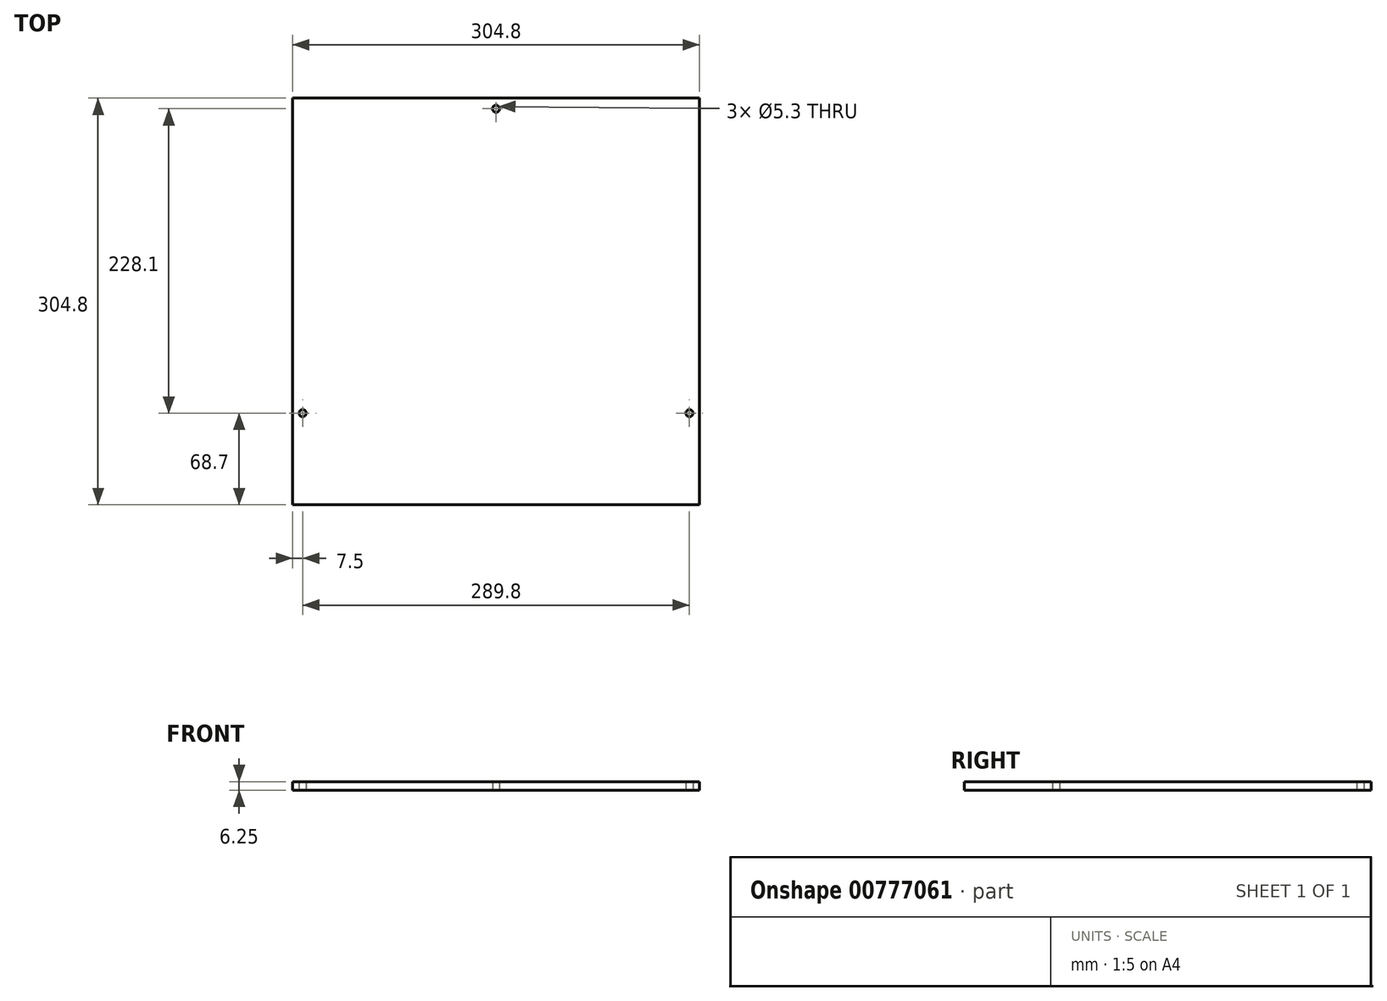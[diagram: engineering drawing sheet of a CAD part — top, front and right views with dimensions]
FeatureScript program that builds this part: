
annotation { "Feature Type Name" : "Feature", "Feature Type Description" : "" }
export const myFeature = defineFeature(function(context is Context, id is Id, definition is map)
    precondition{}
    {
        {
            var Q0;
            Q0=qCreatedBy(makeId("Top.planeOp"),FACE);
            var sketch = newSketch(context, id + "F0", { "sketchPlane" : qUnion([Q0])});
            skLineSegment(sketch, "E0.bottom", {"start": v(-152.4, 152.4) * mm, "end": v(152.4, 152.4) * mm});
            skLineSegment(sketch, "E0.top", {"start": v(-152.4, -152.4) * mm, "end": v(152.4, -152.4) * mm});
            skLineSegment(sketch, "E0.left", {"start": v(-152.4, 152.4) * mm, "end": v(-152.4, -152.4) * mm});
            skLineSegment(sketch, "E0.right", {"start": v(152.4, 152.4) * mm, "end": v(152.4, -152.4) * mm});
            skCircle(sketch, "E1", {"center": v(0, 144.4) * mm, "radius": 2.65 * mm});
            skPoint(sketch, "E1.centerSnap0", {"position": v(0, 152.4) * mm});
            skCircle(sketch, "E2", {"center": v(-144.9, -83.7) * mm, "radius": 2.65 * mm});
            skCircle(sketch, "E3", {"center": v(144.9, -83.7) * mm, "radius": 2.65 * mm});
            skSolve(sketch);
        }
        {
            var Q0;
            Q0=qSketchRegion(id+"F0",true);
            extrude(context, id + "F1", {"entities" : qUnion([Q0]), "depth" : 6.25 * mm});
        }
    });
